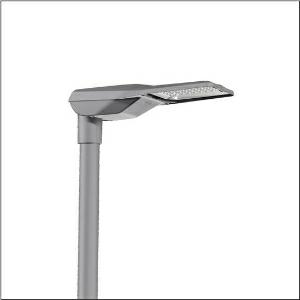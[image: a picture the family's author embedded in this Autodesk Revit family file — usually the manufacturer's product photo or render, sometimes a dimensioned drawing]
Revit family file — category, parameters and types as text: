
# Revit family: streetlight_sl_21_iq_mini___st0_5a_5xe2b41d08gb_120c
name_source: partatom
category: Lighting Fixtures
units: mm (PartAtom-declared; Revit-internal decimal feet)

## family parameters
Cut with Voids When Loaded = No
Host = Face
Light Source = No
Part Type = Normal
Room Calculation Point = No
Round Connector Dimension = Use Diameter
Shared = No

## types (1)
- --- (1 x LED, 5920 lm, 37.1 W, 4000K)
    Apparent Load = 37 VA
    CIE Flux Codes = 41 75 97 100 100
    Color Rendering = 70
    Color Temperature = 4000K
    Default Elevation = 1800 mm
    Description = Streetlight SL 21 iQ mini, mast luminaire, primary light control with lens, of PMMA, primary optical cover: cover, of toughened safety glass, transparent, light distribution: ST0.5a, light emission: direct distribution, primary light characteristic: asymmetric, installation type: post-top, side-entry, LED, High Power LED, rated luminous flux: 5.920lm, luminous efficacy: 160lm/W, light colour: 740, colour temperature: 4000K, control gear: iQ-Comfort, control: Auto-Match, Temp-Guard, Lumen-Switch, Night-Set, Smart-Wire, Light-Fading, Desk-Remote (wireless, voltage-free reading and setting of iQ features in the workshop via application-optimized NFC function/RFID function), optimised constant luminous flux control (CLO 2.0), pre-setting: linear dimming characteristic, mains connection: 220..240V, AC, 50/60Hz, start of lifetime: 37W, end of service life: 39W, reduction: 18W, luminaire housing, of diecast aluminium, powder-coated, Siteco® metallic grey (DB 702S), corrosivity category C5 mid according to DIN EN ISO 12944, please order mast flange separately, inclination adjustable: 0°, 5°, 10°, 15°, sealing non-destructively replaceable, multi-level sealing system, length: 628mm, width: 235mm, height: 110mm, mast flange for spigot size: 42mm (side-entry): 5XC10008XM4, 60/48mm (side-entry/post-top): 5XC10108XM2, 76/60mm (side-entry/post-top): 5XC10108XM1, mounting height: 4..8m, protection rating (complete): IP66, insulation class (complete): insulation class II (safety insulation), certification: CE, ENEC, ENEC+, VDE, impact resistance: IK10, permissible operating ambient temperature for outdoor applications: -40..+50°C, standard-compliant lighting for roads and squares, packaging unit: 1 piece

Light Distribution: ST0.5a
    Height = 110 mm
    Lamp = 1 x LED
    Lamp Light Flux = 5920 lm
    Lamp Power = 37.1 W
    Lamp count = 1
    Length = 625 mm
    Luminous efficacy = 160 lm/W
    Manufacturer = Siteco
    ModVariant = No
    Model = 5XE2B41D08GB
    Number of Poles = 1
    OnlyDefault = Yes
    Power Factor = 1
    Product Name = Streetlight SL 21 iQ mini | ST0.5a
    Product group = mast luminaire | pylon top
    ProductGroupID = 6100
    Protection Class = Protection class II
    Protection Degree = IP 66
    RLX_Detail_Level = 1
    RLX_Emergency_Light_Flux = 0 lm
    RLX_Emergency_Type = 0
    RLX_Emergency_Type_DB = No
    RlxData = <blob elided: 37405 chars, md5=eac9e9ae>
    Socket = socket
    Standby Power = 0 W
    System Light Flux = 5920 lm
    System Power = 37 W
    Type Comments = factory setting: luminous flux: 100 % | dim-lin: 254 | 385 mA
    Type Image = l_1003519.jpg
    URL = http://relux.com
    VarID = @adj_212637
    Voltage = 0 V
    Weight = 0.00 kg
    Width = 234 mm

## geometry (parser evidence)
native form markers: Blend x4, Sweep x11
no freeform markers — native parametric forms only
